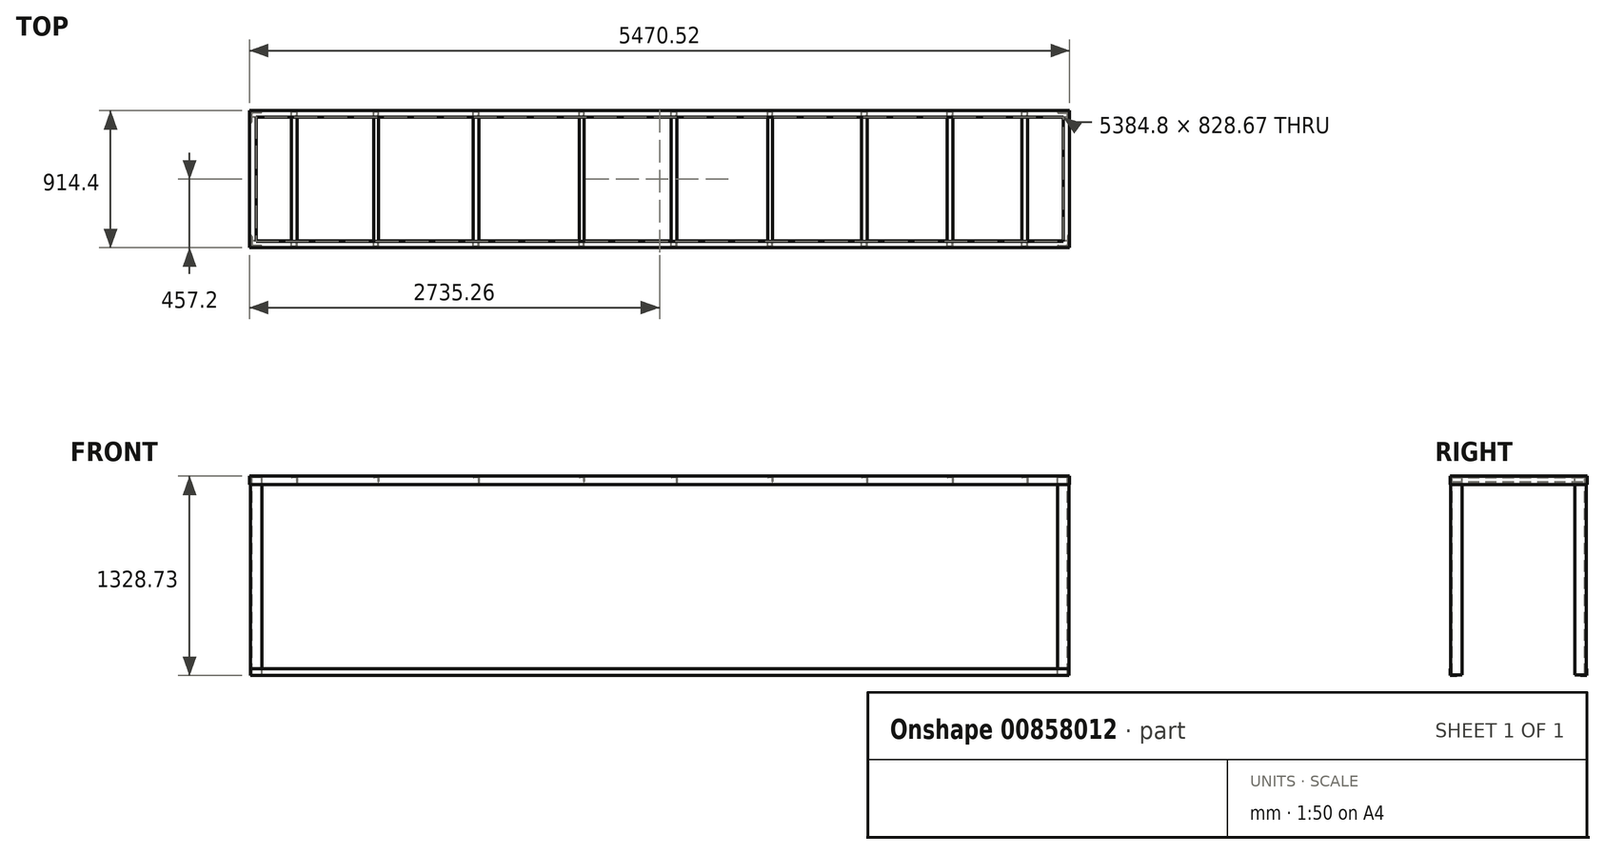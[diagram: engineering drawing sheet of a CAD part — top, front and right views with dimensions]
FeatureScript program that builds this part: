
annotation { "Feature Type Name" : "Feature", "Feature Type Description" : "" }
export const myFeature = defineFeature(function(context is Context, id is Id, definition is map)
    precondition{}
    {
        {
            var Q0;
            Q0=qCreatedBy(makeId("Top.planeOp"),FACE);
            var sketch = newSketch(context, id + "F0", { "sketchPlane" : qUnion([Q0])});
            skLineSegment(sketch, "E0.bottom", {"start": v(2730.5, -452.44) * mm, "end": v(-2730.5, -452.44) * mm});
            skLineSegment(sketch, "E0.top", {"start": v(2730.5, 452.44) * mm, "end": v(-2730.5, 452.44) * mm});
            skLineSegment(sketch, "E0.left", {"start": v(2730.5, -452.44) * mm, "end": v(2730.5, 452.44) * mm});
            skLineSegment(sketch, "E0.right", {"start": v(-2730.5, -452.44) * mm, "end": v(-2730.5, 452.44) * mm});
            skPoint(sketch, "E0.middle", {"position": v(0, 0) * mm});
            skSolve(sketch);
        }
        {
            var Q0;
            Q0=makeQuery(id+"F0.imprint","IMPRINT",FACE,{"disambiguationData":[TD([[makeQuery(id+"F0.imprint","IMPRINT",EDGE,{"derivedFrom":sQuery(id+"F0.wireOp",EDGE,"E0.bottom")}),-1.0]])]});
            var sketch = newSketch(context, id + "F1", { "sketchPlane" : qUnion([Q0])});
            skLineSegment(sketch, "E1.bottom", {"start": v(2730.5, 452.44) * mm, "end": v(2654.3, 452.44) * mm});
            skLineSegment(sketch, "E1.top", {"start": v(2730.5, 376.24) * mm, "end": v(2727.33, 376.24) * mm});
            skLineSegment(sketch, "E1.left", {"start": v(2730.5, 452.44) * mm, "end": v(2730.5, 376.24) * mm});
            skLineSegment(sketch, "E1.right", {"start": v(2654.3, 452.44) * mm, "end": v(2654.3, 449.26) * mm});
            skLineSegment(sketch, "E2.top", {"start": v(2660.65, 442.91) * mm, "end": v(2714.63, 442.91) * mm});
            skLineSegment(sketch, "E2.right", {"start": v(2720.98, 382.59) * mm, "end": v(2720.98, 436.56) * mm});
            skPoint(sketch, "E3.visualSharp", {"position": v(2654.3, 442.91) * mm});
            skArc(sketch, "E3.filletArc", {"start": v(2654.3, 449.26) * mm, "mid": v(2656.16, 444.77) * mm, "end": v(2660.65, 442.91) * mm});
            skPoint(sketch, "E4.visualSharp", {"position": v(2720.98, 442.91) * mm});
            skArc(sketch, "E4.filletArc", {"start": v(2720.98, 436.56) * mm, "mid": v(2719.12, 441.05) * mm, "end": v(2714.63, 442.91) * mm});
            skPoint(sketch, "E5.visualSharp", {"position": v(2720.98, 376.24) * mm});
            skArc(sketch, "E5.filletArc", {"start": v(2720.98, 382.59) * mm, "mid": v(2722.83, 378.1) * mm, "end": v(2727.33, 376.24) * mm});
            skSolve(sketch);
        }
        {
            var Q0;
            Q0=makeQuery(id+"F1.imprint","IMPRINT",FACE,{"disambiguationData":[TD([[makeQuery(id+"F1.imprint","IMPRINT",EDGE,{"derivedFrom":sQuery(id+"F1.wireOp",EDGE,"E1.bottom")}),1.0]])]});
            extrude(context, id + "F2", {"entities" : qUnion([Q0]), "oppositeDirection" : true, "depth" : 1320.8 * mm, "offsetDistance" : 25.4 * mm});
        }
        {
            var Q0;
            Q0=makeQuery(id+"F2.opExtrude","SWEPT_BODY",BODY,{"disambiguationData":[OSD([sQuery(id+"F1.wireOp",EDGE,"E1.bottom"),sQuery(id+"F1.wireOp",EDGE,"E1.top"),sQuery(id+"F1.wireOp",EDGE,"E1.left"),sQuery(id+"F1.wireOp",EDGE,"E1.right"),sQuery(id+"F1.wireOp",EDGE,"E2.top"),sQuery(id+"F1.wireOp",EDGE,"E2.right"),sQuery(id+"F1.wireOp",EDGE,"E3.filletArc"),sQuery(id+"F1.wireOp",EDGE,"E4.filletArc"),sQuery(id+"F1.wireOp",EDGE,"E5.filletArc")])]});
            var Q1;
            Q1=qCreatedBy(makeId("Right.planeOp"),FACE);
            mirror(context, id + "F3", {"entities" : qUnion([Q0]), "mirrorPlane" : qUnion([Q1])});
        }
        {
            var Q0;
            Q0=makeQuery(id+"F3.opPattern","COPY",BODY,{"derivedFrom":makeQuery(id+"F2.opExtrude","SWEPT_BODY",BODY,{"disambiguationData":[OSD([sQuery(id+"F1.wireOp",EDGE,"E1.bottom"),sQuery(id+"F1.wireOp",EDGE,"E1.top"),sQuery(id+"F1.wireOp",EDGE,"E1.left"),sQuery(id+"F1.wireOp",EDGE,"E1.right"),sQuery(id+"F1.wireOp",EDGE,"E2.top"),sQuery(id+"F1.wireOp",EDGE,"E2.right"),sQuery(id+"F1.wireOp",EDGE,"E3.filletArc"),sQuery(id+"F1.wireOp",EDGE,"E4.filletArc"),sQuery(id+"F1.wireOp",EDGE,"E5.filletArc")])]}),"instanceName":"1"});
            var Q1;
            Q1=makeQuery(id+"F2.opExtrude","SWEPT_BODY",BODY,{"disambiguationData":[OSD([sQuery(id+"F1.wireOp",EDGE,"E1.bottom"),sQuery(id+"F1.wireOp",EDGE,"E1.top"),sQuery(id+"F1.wireOp",EDGE,"E1.left"),sQuery(id+"F1.wireOp",EDGE,"E1.right"),sQuery(id+"F1.wireOp",EDGE,"E2.top"),sQuery(id+"F1.wireOp",EDGE,"E2.right"),sQuery(id+"F1.wireOp",EDGE,"E3.filletArc"),sQuery(id+"F1.wireOp",EDGE,"E4.filletArc"),sQuery(id+"F1.wireOp",EDGE,"E5.filletArc")])]});
            var Q2;
            Q2=qCreatedBy(makeId("Front.planeOp"),FACE);
            mirror(context, id + "F4", {"entities" : qUnion([Q0, Q1]), "mirrorPlane" : qUnion([Q2])});
        }
        {
            var Q0;
            Q0=makeQuery(id+"F4.opPattern","COPY",FACE,{"derivedFrom":makeQuery(id+"F3.opPattern","COPY",FACE,{"derivedFrom":makeQuery(id+"F2.opExtrude","SWEPT_FACE",FACE,{"disambiguationData":[OSD([sQuery(id+"F1.wireOp",EDGE,"E1.bottom")])]}),"instanceName":"1"}),"instanceName":"1"});
            var sketch = newSketch(context, id + "F5", { "sketchPlane" : qUnion([Q0])});
            skLineSegment(sketch, "E6.bottom", {"start": v(-2730.5, 0) * mm, "end": v(-2692.4, 0) * mm});
            skLineSegment(sketch, "E6.left", {"start": v(-2730.5, 0) * mm, "end": v(-2730.5, -50.8) * mm});
            skLineSegment(sketch, "E7.0", {"start": v(-2692.4, 4.76) * mm, "end": v(-2735.26, 4.76) * mm});
            skLineSegment(sketch, "E8.0", {"start": v(-2735.26, 4.76) * mm, "end": v(-2735.26, -50.8) * mm});
            skLineSegment(sketch, "E9.filletArc", {"start": v(-2735.26, 4.76) * mm, "end": v(-2735.26, 4.76) * mm});
            skLineSegment(sketch, "E10", {"start": v(-2692.4, 0) * mm, "end": v(-2692.4, 4.76) * mm});
            skLineSegment(sketch, "E11", {"start": v(-2730.5, -50.8) * mm, "end": v(-2735.26, -50.8) * mm});
            skSolve(sketch);
        }
        {
            var Q0;
            Q0=makeQuery(id+"F5.imprint","IMPRINT",FACE,{"disambiguationData":[TD([[makeQuery(id+"F5.imprint","IMPRINT",EDGE,{"derivedFrom":sQuery(id+"F5.wireOp",EDGE,"E6.bottom")}),1.0]])]});
            var Q1;
            Q1=sQuery(id+"F0.wireOp",EDGE,"E0.right");
            var Q2;
            Q2=sQuery(id+"F0.wireOp",EDGE,"E0.top");
            var Q3;
            Q3=sQuery(id+"F0.wireOp",EDGE,"E0.left");
            var Q4;
            Q4=sQuery(id+"F0.wireOp",EDGE,"E0.bottom");
            sweep(context, id + "F6", {"profiles" : qUnion([Q0]), "path" : qUnion([Q1, Q2, Q3, Q4])});
        }
        {
            var Q0;
            Q0=makeQuery(id+"F4.opPattern","COPY",FACE,{"derivedFrom":makeQuery(id+"F3.opPattern","COPY",FACE,{"derivedFrom":makeQuery(id+"F2.opExtrude","SWEPT_FACE",FACE,{"disambiguationData":[OSD([sQuery(id+"F1.wireOp",EDGE,"E1.left")])]}),"instanceName":"1"}),"instanceName":"1"});
            var sketch = newSketch(context, id + "F7", { "sketchPlane" : qUnion([Q0])});
            skLineSegment(sketch, "E12.bottom", {"start": v(452.44, -1320.8) * mm, "end": v(415.43, -1320.8) * mm});
            skLineSegment(sketch, "E12.left", {"start": v(452.44, -1320.8) * mm, "end": v(452.44, -1283.45) * mm});
            skLineSegment(sketch, "E13.0", {"start": v(455.61, -1323.98) * mm, "end": v(455.61, -1280.27) * mm});
            skLineSegment(sketch, "E14.0", {"start": v(455.61, -1323.98) * mm, "end": v(412.26, -1323.98) * mm});
            skLineSegment(sketch, "E15.filletArc", {"start": v(455.61, -1323.98) * mm, "end": v(455.61, -1323.98) * mm});
            skLineSegment(sketch, "E16", {"start": v(455.61, -1280.27) * mm, "end": v(455.61, -1280.27) * mm});
            skLineSegment(sketch, "E17", {"start": v(412.26, -1323.98) * mm, "end": v(412.26, -1323.98) * mm});
            skPoint(sketch, "E18.visualSharp", {"position": v(412.26, -1320.8) * mm});
            skArc(sketch, "E18.filletArc", {"start": v(415.43, -1320.8) * mm, "mid": v(413.19, -1321.73) * mm, "end": v(412.26, -1323.98) * mm});
            skPoint(sketch, "E19.visualSharp", {"position": v(452.44, -1280.27) * mm});
            skArc(sketch, "E19.filletArc", {"start": v(455.61, -1280.27) * mm, "mid": v(453.37, -1281.2) * mm, "end": v(452.44, -1283.45) * mm});
            skSolve(sketch);
        }
        {
            var Q0;
            Q0=makeQuery(id+"F7.imprint","IMPRINT",FACE,{"disambiguationData":[TD([[makeQuery(id+"F7.imprint","IMPRINT",EDGE,{"derivedFrom":sQuery(id+"F7.wireOp",EDGE,"E12.bottom")}),-1.0]])]});
            extrude(context, id + "F8", {"entities" : qUnion([Q0]), "oppositeDirection" : true, "depth" : 5461 * mm, "offsetDistance" : 25.4 * mm});
        }
        {
            var Q0;
            Q0=makeQuery(id+"F8.opExtrude","SWEPT_BODY",BODY,{"disambiguationData":[OSD([sQuery(id+"F7.wireOp",EDGE,"E12.bottom"),sQuery(id+"F7.wireOp",EDGE,"E12.left"),sQuery(id+"F7.wireOp",EDGE,"E13.0"),sQuery(id+"F7.wireOp",EDGE,"E14.0"),sQuery(id+"F7.wireOp",EDGE,"E18.filletArc"),sQuery(id+"F7.wireOp",EDGE,"E19.filletArc")])]});
            var Q1;
            Q1=qCreatedBy(makeId("Front.planeOp"),FACE);
            mirror(context, id + "F9", {"entities" : qUnion([Q0]), "mirrorPlane" : qUnion([Q1])});
        }
        {
            var Q0;
            Q0=makeQuery(id+"F6.opSweep","SWEPT_FACE",FACE,{"disambiguationData":[OSD([sQuery(id+"F0.wireOp",EDGE,"E0.top"),sQuery(id+"F5.wireOp",EDGE,"E6.left")])]});
            var sketch = newSketch(context, id + "F10", { "sketchPlane" : qUnion([Q0])});
            skLineSegment(sketch, "E20.bottom", {"start": v(-2417.76, 0) * mm, "end": v(-2455.86, 0) * mm});
            skLineSegment(sketch, "E20.top", {"start": v(-2417.76, -38.1) * mm, "end": v(-2417.76, -38.1) * mm});
            skLineSegment(sketch, "E20.left", {"start": v(-2417.76, 0) * mm, "end": v(-2417.76, -38.1) * mm});
            skLineSegment(sketch, "E20.right", {"start": v(-2455.86, 0) * mm, "end": v(-2455.86, 0) * mm});
            skLineSegment(sketch, "E21.0", {"start": v(-2420.94, -3.18) * mm, "end": v(-2420.94, -34.92) * mm});
            skLineSegment(sketch, "E21.1", {"start": v(-2420.94, -3.18) * mm, "end": v(-2452.69, -3.18) * mm});
            skPoint(sketch, "E22.visualSharp", {"position": v(-2455.86, -3.18) * mm});
            skArc(sketch, "E22.filletArc", {"start": v(-2455.86, 0) * mm, "mid": v(-2454.93, -2.25) * mm, "end": v(-2452.69, -3.18) * mm});
            skPoint(sketch, "E23.visualSharp", {"position": v(-2420.94, -38.1) * mm});
            skArc(sketch, "E23.filletArc", {"start": v(-2420.94, -34.92) * mm, "mid": v(-2420, -37.17) * mm, "end": v(-2417.76, -38.1) * mm});
            skLineSegment(sketch, "E24.bottom", {"start": v(-1874.84, 0) * mm, "end": v(-1906.59, 0) * mm});
            skLineSegment(sketch, "E24.top", {"start": v(-1874.84, -31.75) * mm, "end": v(-1874.84, -31.75) * mm});
            skLineSegment(sketch, "E24.left", {"start": v(-1874.84, 0) * mm, "end": v(-1874.84, -31.75) * mm});
            skLineSegment(sketch, "E24.right", {"start": v(-1906.59, 0) * mm, "end": v(-1906.59, 0) * mm});
            skLineSegment(sketch, "E25.0", {"start": v(-1878.01, -6.35) * mm, "end": v(-1878.01, -28.57) * mm});
            skLineSegment(sketch, "E26.0", {"start": v(-1881.19, -3.17) * mm, "end": v(-1903.41, -3.17) * mm});
            skPoint(sketch, "E27.visualSharp", {"position": v(-1906.59, -3.17) * mm});
            skArc(sketch, "E27.filletArc", {"start": v(-1906.59, 0) * mm, "mid": v(-1905.66, -2.25) * mm, "end": v(-1903.41, -3.17) * mm});
            skPoint(sketch, "E28.visualSharp", {"position": v(-1878.01, -3.17) * mm});
            skArc(sketch, "E28.filletArc", {"start": v(-1878.01, -6.35) * mm, "mid": v(-1878.94, -4.1) * mm, "end": v(-1881.19, -3.17) * mm});
            skPoint(sketch, "E29.visualSharp", {"position": v(-1878.01, -31.75) * mm});
            skArc(sketch, "E29.filletArc", {"start": v(-1878.01, -28.57) * mm, "mid": v(-1877.08, -30.82) * mm, "end": v(-1874.84, -31.75) * mm});
            skLineSegment(sketch, "E30", {"start": v(-1878.01, -28.57) * mm, "end": v(-1878.01, -31.75) * mm});
            skPoint(sketch, "E31.start.orphan", {"position": v(-1878.01, -38.1) * mm});
            skSolve(sketch);
        }
        {
            var Q0;
            Q0 = qSketchRegion(id + "F10", true);
            extrude(context, id + "F11", {"entities" : qUnion([Q0]), "depth" : 904.24 * mm, "offsetDistance" : 25.4 * mm});
        }
        {
            var Q0;
            Q0=makeQuery(id+"F11.opExtrude","SWEPT_BODY",BODY,{"disambiguationData":[OSD([sQuery(id+"F10.wireOp",EDGE,"E20.bottom"),sQuery(id+"F10.wireOp",EDGE,"E20.left"),sQuery(id+"F10.wireOp",EDGE,"E21.0"),sQuery(id+"F10.wireOp",EDGE,"E21.1"),sQuery(id+"F10.wireOp",EDGE,"E22.filletArc"),sQuery(id+"F10.wireOp",EDGE,"E23.filletArc")])]});
            var Q1;
            Q1=makeQuery(id+"F6.opSweep","SWEPT_EDGE",EDGE,{"disambiguationData":[OSD([sQuery(id+"F0.wireOp",EDGE,"E0.top"),sQuery(id+"F1.wireOp",EDGE,"E1.bottom"),sQuery(id+"F1.wireOp",EDGE,"E1.left"),sQuery(id+"F5.wireOp",EDGE,"E6.left"),sQuery(id+"F5.wireOp",EDGE,"E11")])]});
            transform(context, id + "F12", {"entities" : qUnion([Q0]), "transformType" : TransformType.TRANSLATION_DISTANCE, "transformDirection" : qUnion([Q1]), "distance" : 1212.85 * mm, "makeCopy" : true});
        }
        {
            var Q0;
            Q0=makeQuery(id+"F11.opExtrude","SWEPT_BODY",BODY,{"disambiguationData":[OSD([sQuery(id+"F10.wireOp",EDGE,"E24.bottom"),sQuery(id+"F10.wireOp",EDGE,"E24.left"),sQuery(id+"F10.wireOp",EDGE,"E25.0"),sQuery(id+"F10.wireOp",EDGE,"E26.0"),sQuery(id+"F10.wireOp",EDGE,"E27.filletArc"),sQuery(id+"F10.wireOp",EDGE,"E28.filletArc"),sQuery(id+"F10.wireOp",EDGE,"E29.filletArc")])]});
            var Q1;
            Q1=makeQuery(id+"F6.opSweep","SWEPT_EDGE",EDGE,{"disambiguationData":[OSD([sQuery(id+"F0.wireOp",EDGE,"E0.top"),sQuery(id+"F1.wireOp",EDGE,"E1.bottom"),sQuery(id+"F5.wireOp",EDGE,"E6.bottom"),sQuery(id+"F5.wireOp",EDGE,"E10")])]});
            var Q2;
            Q2=makeQuery(id+"F6.opSweep","SWEPT_EDGE",EDGE,{"disambiguationData":[OSD([sQuery(id+"F0.wireOp",EDGE,"E0.top"),sQuery(id+"F5.wireOp",EDGE,"E7.0"),sQuery(id+"F5.wireOp",EDGE,"E10")])]});
            transform(context, id + "F13", {"entities" : qUnion([Q0]), "transformType" : TransformType.TRANSLATION_DISTANCE, "transformDirection" : qUnion([Q2]), "distance" : 1371.6 * mm, "makeCopy" : true});
        }
        {
            var Q0;
            Q0=makeQuery(id+"F12.opPattern","COPY",BODY,{"derivedFrom":makeQuery(id+"F11.opExtrude","SWEPT_BODY",BODY,{"disambiguationData":[OSD([sQuery(id+"F10.wireOp",EDGE,"E20.bottom"),sQuery(id+"F10.wireOp",EDGE,"E20.left"),sQuery(id+"F10.wireOp",EDGE,"E21.0"),sQuery(id+"F10.wireOp",EDGE,"E21.1"),sQuery(id+"F10.wireOp",EDGE,"E22.filletArc"),sQuery(id+"F10.wireOp",EDGE,"E23.filletArc")])]}),"instanceName":"1"});
            var Q1;
            Q1=makeQuery(id+"F6.opSweep","SWEPT_EDGE",EDGE,{"disambiguationData":[OSD([sQuery(id+"F0.wireOp",EDGE,"E0.top"),sQuery(id+"F1.wireOp",EDGE,"E1.bottom"),sQuery(id+"F5.wireOp",EDGE,"E6.bottom"),sQuery(id+"F5.wireOp",EDGE,"E10")])]});
            transform(context, id + "F14", {"entities" : qUnion([Q0]), "transformType" : TransformType.TRANSLATION_DISTANCE, "transformDirection" : qUnion([Q1]), "distance" : 1320.8 * mm, "makeCopy" : true});
        }
        {
            var Q0;
            Q0=makeQuery(id+"F13.opPattern","COPY",BODY,{"derivedFrom":makeQuery(id+"F11.opExtrude","SWEPT_BODY",BODY,{"disambiguationData":[OSD([sQuery(id+"F10.wireOp",EDGE,"E24.bottom"),sQuery(id+"F10.wireOp",EDGE,"E24.left"),sQuery(id+"F10.wireOp",EDGE,"E25.0"),sQuery(id+"F10.wireOp",EDGE,"E26.0"),sQuery(id+"F10.wireOp",EDGE,"E27.filletArc"),sQuery(id+"F10.wireOp",EDGE,"E28.filletArc"),sQuery(id+"F10.wireOp",EDGE,"E29.filletArc")])]}),"instanceName":"1"});
            var Q1;
            Q1=makeQuery(id+"F6.opSweep","SWEPT_EDGE",EDGE,{"disambiguationData":[OSD([sQuery(id+"F0.wireOp",EDGE,"E0.top"),sQuery(id+"F5.wireOp",EDGE,"E7.0"),sQuery(id+"F5.wireOp",EDGE,"E8.0")])]});
            transform(context, id + "F15", {"entities" : qUnion([Q0]), "transformType" : TransformType.TRANSLATION_DISTANCE, "transformDirection" : qUnion([Q1]), "distance" : 1257.3 * mm, "makeCopy" : true});
        }
        {
            var Q0;
            Q0=makeQuery(id+"F14.opPattern","COPY",BODY,{"derivedFrom":makeQuery(id+"F12.opPattern","COPY",BODY,{"derivedFrom":makeQuery(id+"F11.opExtrude","SWEPT_BODY",BODY,{"disambiguationData":[OSD([sQuery(id+"F10.wireOp",EDGE,"E20.bottom"),sQuery(id+"F10.wireOp",EDGE,"E20.left"),sQuery(id+"F10.wireOp",EDGE,"E21.0"),sQuery(id+"F10.wireOp",EDGE,"E21.1"),sQuery(id+"F10.wireOp",EDGE,"E22.filletArc"),sQuery(id+"F10.wireOp",EDGE,"E23.filletArc")])]}),"instanceName":"1"}),"instanceName":"1"});
            var Q1;
            Q1=makeQuery(id+"F6.opSweep","SWEPT_EDGE",EDGE,{"disambiguationData":[OSD([sQuery(id+"F0.wireOp",EDGE,"E0.top"),sQuery(id+"F5.wireOp",EDGE,"E7.0"),sQuery(id+"F5.wireOp",EDGE,"E8.0")])]});
            transform(context, id + "F16", {"entities" : qUnion([Q0]), "transformType" : TransformType.TRANSLATION_DISTANCE, "transformDirection" : qUnion([Q1]), "distance" : 1270 * mm, "makeCopy" : true});
        }
        {
            var Q0;
            Q0=makeQuery(id+"F16.opPattern","COPY",BODY,{"derivedFrom":makeQuery(id+"F14.opPattern","COPY",BODY,{"derivedFrom":makeQuery(id+"F12.opPattern","COPY",BODY,{"derivedFrom":makeQuery(id+"F11.opExtrude","SWEPT_BODY",BODY,{"disambiguationData":[OSD([sQuery(id+"F10.wireOp",EDGE,"E20.bottom"),sQuery(id+"F10.wireOp",EDGE,"E20.left"),sQuery(id+"F10.wireOp",EDGE,"E21.0"),sQuery(id+"F10.wireOp",EDGE,"E21.1"),sQuery(id+"F10.wireOp",EDGE,"E22.filletArc"),sQuery(id+"F10.wireOp",EDGE,"E23.filletArc")])]}),"instanceName":"1"}),"instanceName":"1"}),"instanceName":"1"});
            var Q1;
            Q1=makeQuery(id+"F6.opSweep","SWEPT_EDGE",EDGE,{"disambiguationData":[OSD([sQuery(id+"F0.wireOp",EDGE,"E0.top"),sQuery(id+"F5.wireOp",EDGE,"E7.0"),sQuery(id+"F5.wireOp",EDGE,"E8.0")])]});
            transform(context, id + "F17", {"entities" : qUnion([Q0]), "transformType" : TransformType.TRANSLATION_DISTANCE, "transformDirection" : qUnion([Q1]), "distance" : 571.5 * mm, "makeCopy" : true});
        }
        {
            var Q0;
            Q0=makeQuery(id+"F17.opPattern","COPY",BODY,{"derivedFrom":makeQuery(id+"F16.opPattern","COPY",BODY,{"derivedFrom":makeQuery(id+"F14.opPattern","COPY",BODY,{"derivedFrom":makeQuery(id+"F12.opPattern","COPY",BODY,{"derivedFrom":makeQuery(id+"F11.opExtrude","SWEPT_BODY",BODY,{"disambiguationData":[OSD([sQuery(id+"F10.wireOp",EDGE,"E20.bottom"),sQuery(id+"F10.wireOp",EDGE,"E20.left"),sQuery(id+"F10.wireOp",EDGE,"E21.0"),sQuery(id+"F10.wireOp",EDGE,"E21.1"),sQuery(id+"F10.wireOp",EDGE,"E22.filletArc"),sQuery(id+"F10.wireOp",EDGE,"E23.filletArc")])]}),"instanceName":"1"}),"instanceName":"1"}),"instanceName":"1"}),"instanceName":"1"});
            var Q1;
            Q1=makeQuery(id+"F6.opSweep","SWEPT_EDGE",EDGE,{"disambiguationData":[OSD([sQuery(id+"F0.wireOp",EDGE,"E0.top"),sQuery(id+"F1.wireOp",EDGE,"E1.bottom"),sQuery(id+"F5.wireOp",EDGE,"E6.bottom"),sQuery(id+"F5.wireOp",EDGE,"E10")])]});
            transform(context, id + "F18", {"entities" : qUnion([Q0]), "transformType" : TransformType.TRANSLATION_DISTANCE, "transformDirection" : qUnion([Q1]), "distance" : 498.5 * mm, "makeCopy" : true});
        }
    });
